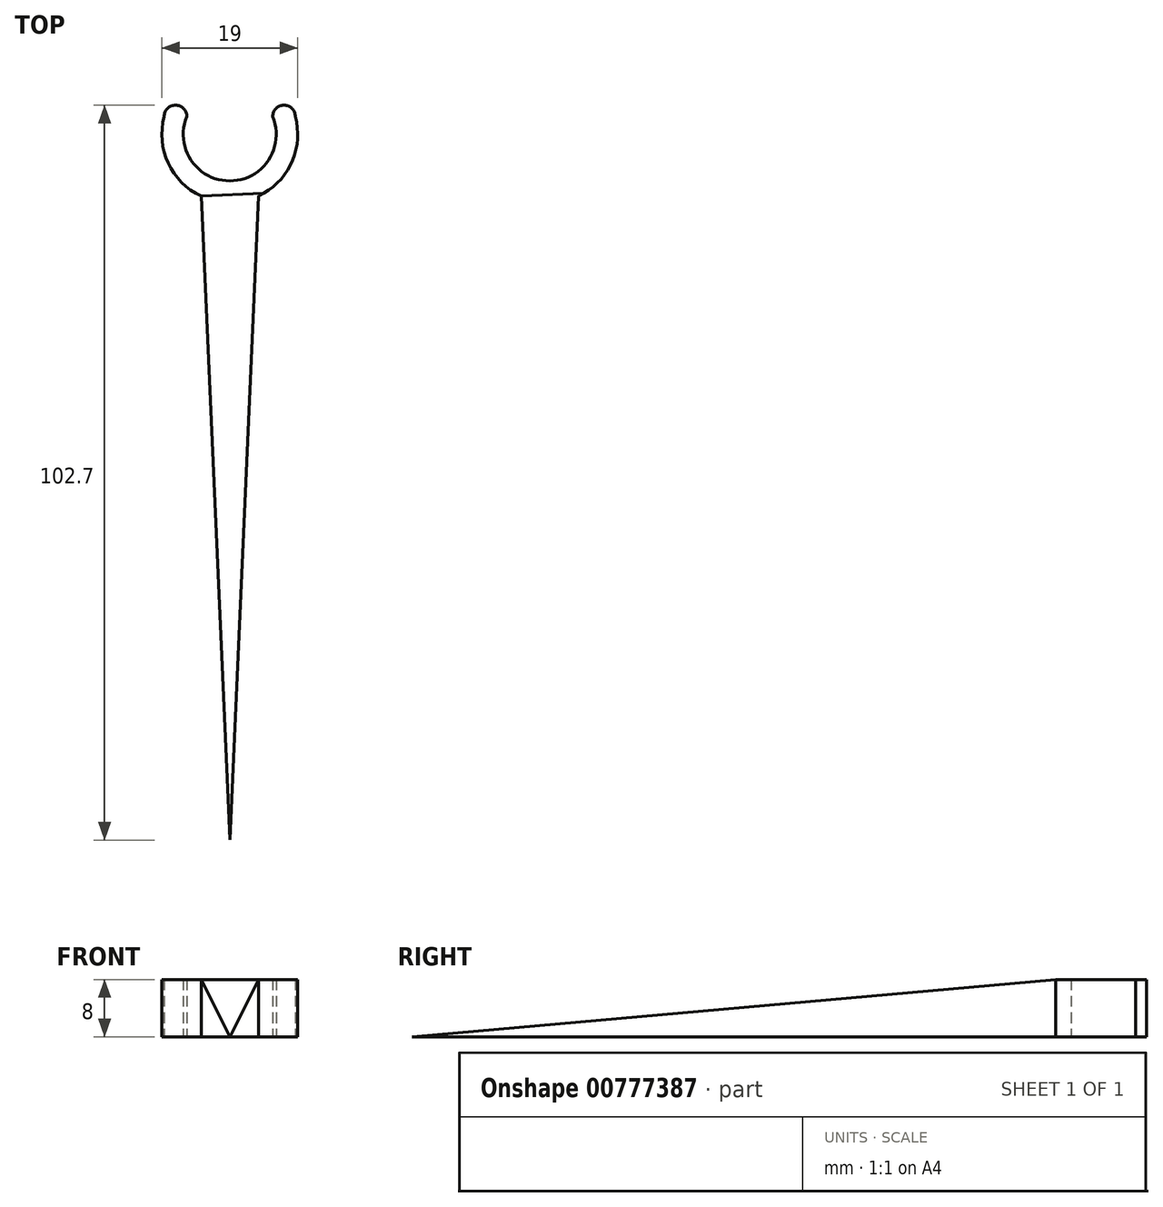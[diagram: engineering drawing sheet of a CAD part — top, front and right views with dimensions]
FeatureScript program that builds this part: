
annotation { "Feature Type Name" : "Feature", "Feature Type Description" : "" }
export const myFeature = defineFeature(function(context is Context, id is Id, definition is map)
    precondition{}
    {
        {
            var Q0;
            Q0=qCreatedBy(makeId("Top.planeOp"),FACE);
            var sketch = newSketch(context, id + "F0", { "sketchPlane" : qUnion([Q0])});
            skArc(sketch, "E0", {"start": v(-6, 2.5) * mm, "mid": v(0, -6.5) * mm, "end": v(6, 2.5) * mm});
            skArc(sketch, "E1", {"start": v(-6, 2.5) * mm, "mid": v(-7.58, 4.08) * mm, "end": v(-9.17, 2.5) * mm});
            skArc(sketch, "E2", {"start": v(6, 2.5) * mm, "mid": v(7.58, 4.08) * mm, "end": v(9.17, 2.5) * mm});
            skArc(sketch, "E3", {"start": v(-9.17, 2.5) * mm, "mid": v(-8.62, -4) * mm, "end": v(-4, -8.62) * mm});
            skArc(sketch, "E4", {"start": v(9.17, 2.5) * mm, "mid": v(8.62, -4) * mm, "end": v(4, -8.62) * mm});
            skLineSegment(sketch, "E5", {"start": v(-4, -8.62) * mm, "end": v(0, -98.62) * mm});
            skLineSegment(sketch, "E6", {"start": v(0, -98.62) * mm, "end": v(4, -8.62) * mm});
            skSolve(sketch);
        }
        {
            var Q0;
            Q0 = qSketchRegion(id + "F0", true);
            extrude(context, id + "F1", {"entities" : qUnion([Q0]), "depth" : 8 * mm, "offsetDistance" : 25 * mm});
        }
        {
            var Q0;
            Q0=makeQuery(id+"F1.opExtrude","SWEPT_FACE",FACE,{"disambiguationData":[OSD([sQuery(id+"F0.wireOp",EDGE,"E5")])]});
            var sketch = newSketch(context, id + "F2", { "sketchPlane" : qUnion([Q0])});
            skLineSegment(sketch, "E7", {"start": v(8.43, 8) * mm, "end": v(98.52, 0) * mm});
            skLineSegment(sketch, "E8", {"start": v(98.52, 0) * mm, "end": v(8.43, 0) * mm});
            skLineSegment(sketch, "E9", {"start": v(98.52, 0) * mm, "end": v(98.52, 0) * mm});
            skLineSegment(sketch, "E10", {"start": v(8.43, 8) * mm, "end": v(-8.57, 8) * mm});
            skLineSegment(sketch, "E11", {"start": v(-8.57, 8) * mm, "end": v(-8.57, 0) * mm});
            skLineSegment(sketch, "E12", {"start": v(-8.57, 0) * mm, "end": v(8.43, 0) * mm});
            skSolve(sketch);
        }
        {
            var Q0;
            Q0 = qSketchRegion(id + "F2", true);
            extrude(context, id + "F3", {"entities" : qUnion([Q0]), "operationType" : NewBodyOperationType.INTERSECT, "endBound" : BoundingType.SYMMETRIC, "depth" : 30 * mm, "offsetDistance" : 25 * mm});
        }
    });
